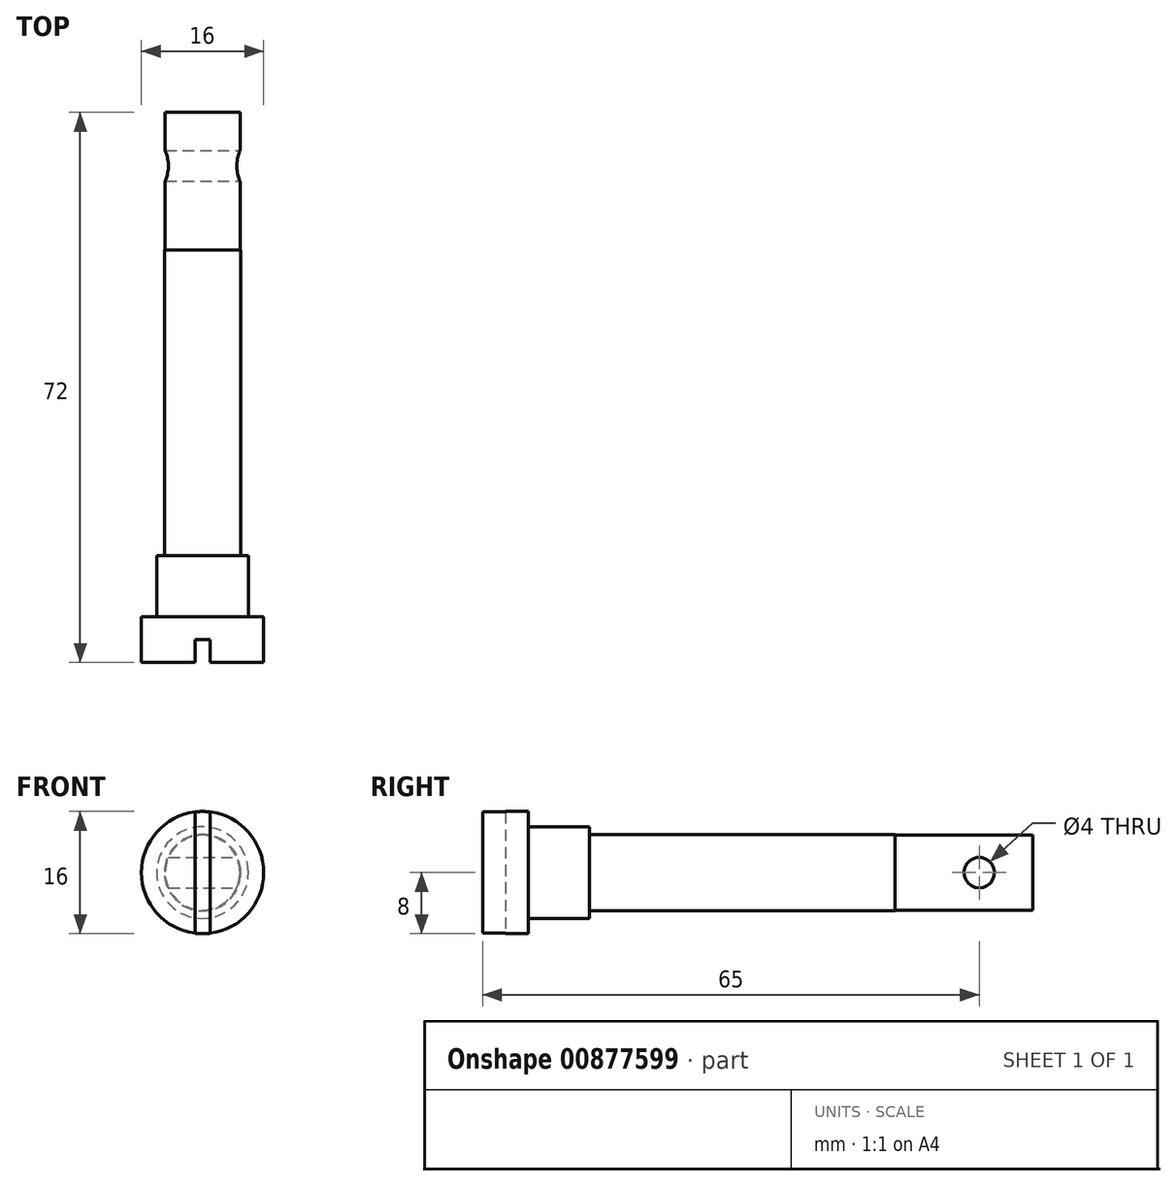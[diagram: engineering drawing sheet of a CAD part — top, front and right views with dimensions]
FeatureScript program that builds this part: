
annotation { "Feature Type Name" : "Feature", "Feature Type Description" : "" }
export const myFeature = defineFeature(function(context is Context, id is Id, definition is map)
    precondition{}
    {
        {
            var Q0;
            Q0=qCreatedBy(makeId("Right.planeOp"),FACE);
            var sketch = newSketch(context, id + "F0", { "sketchPlane" : qUnion([Q0])});
            skLineSegment(sketch, "E0", {"start": v(-20, 0) * mm, "end": v(-20, 8) * mm});
            skLineSegment(sketch, "E1", {"start": v(-20, 8) * mm, "end": v(-14, 8) * mm});
            skLineSegment(sketch, "E2", {"start": v(-14, 8) * mm, "end": v(-14, 6) * mm});
            skLineSegment(sketch, "E3", {"start": v(-6, 5) * mm, "end": v(34, 5) * mm});
            skLineSegment(sketch, "E4", {"start": v(34, 5) * mm, "end": v(34, 4.9) * mm});
            skLineSegment(sketch, "E5", {"start": v(34, 4.9) * mm, "end": v(52, 4.9) * mm});
            skLineSegment(sketch, "E6", {"start": v(52, 4.9) * mm, "end": v(52, 0) * mm});
            skLineSegment(sketch, "E7", {"start": v(52, 0) * mm, "end": v(-20, 0) * mm});
            skLineSegment(sketch, "E8", {"start": v(-27.35, 0) * mm, "end": v(70.3, 0) * mm, "construction": true});
            skLineSegment(sketch, "E9", {"start": v(-14, 6) * mm, "end": v(-6, 6) * mm});
            skLineSegment(sketch, "E10", {"start": v(-6, 6) * mm, "end": v(-6, 5) * mm});
            skSolve(sketch);
        }
        {
            var Q0;
            Q0=qSketchRegion(id+"F0",true);
            var Q1;
            Q1=sQuery(id+"F0.wireOp",EDGE,"E8");
            revolve(context, id + "F1", {"surfaceOperationType" : NewSurfaceOperationType.NEW, "entities" : qUnion([Q0]), "axis" : qUnion([Q1]), "revolveType" : RevolveType.FULL});
        }
        {
            var Q0;
            Q0=makeQuery(id+"F1.opRevolve","SWEPT_FACE",FACE,{"disambiguationData":[OSD([sQuery(id+"F0.wireOp",EDGE,"E0")])]});
            var sketch = newSketch(context, id + "F2", { "sketchPlane" : qUnion([Q0])});
            skLineSegment(sketch, "E11.bottom", {"start": v(1, 9) * mm, "end": v(-1, 9) * mm});
            skLineSegment(sketch, "E11.top", {"start": v(1, -9) * mm, "end": v(-1, -9) * mm});
            skLineSegment(sketch, "E11.left", {"start": v(1, 9) * mm, "end": v(1, -9) * mm});
            skLineSegment(sketch, "E11.right", {"start": v(-1, 9) * mm, "end": v(-1, -9) * mm});
            skPoint(sketch, "E11.middle", {"position": v(0, 0) * mm});
            skSolve(sketch);
        }
        {
            var Q0;
            Q0=qSketchRegion(id+"F2",true);
            extrude(context, id + "F3", {"entities" : qUnion([Q0]), "operationType" : NewBodyOperationType.REMOVE, "oppositeDirection" : true, "depth" : 3 * mm, "offsetDistance" : 25 * mm});
        }
        {
            var Q0;
            Q0=qCreatedBy(makeId("Right.planeOp"),FACE);
            var sketch = newSketch(context, id + "F4", { "sketchPlane" : qUnion([Q0])});
            skCircle(sketch, "E12", {"center": v(45, 0) * mm, "radius": 2 * mm});
            skSolve(sketch);
        }
        {
            var Q0;
            Q0=qSketchRegion(id+"F4",true);
            extrude(context, id + "F5", {"entities" : qUnion([Q0]), "operationType" : NewBodyOperationType.REMOVE, "endBound" : BoundingType.SYMMETRIC, "oppositeDirection" : true, "depth" : 25 * mm, "offsetDistance" : 25 * mm});
        }
    });
